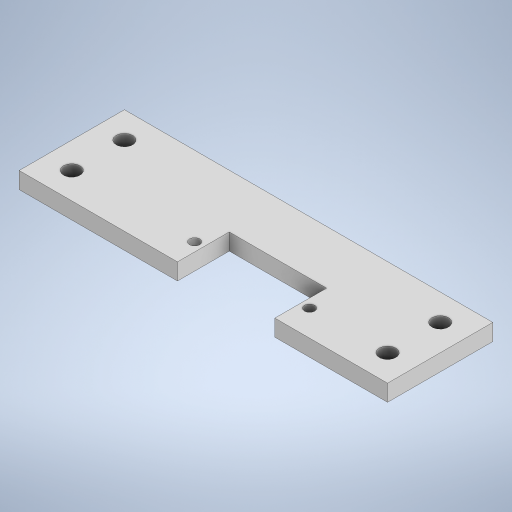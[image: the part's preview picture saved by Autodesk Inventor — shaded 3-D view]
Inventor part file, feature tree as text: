
AUTODESK INVENTOR PART (.ipt)
format: ipt  version: 2023.1 (Build 271208000, 208)  size: 259,584 bytes
history: native  units: mm
features: extrude x1, sketch x1
ambient origin geometry x8: Origin, YZ Plane, XZ Plane, XY Plane, X Axis, Y Axis, Z Axis, Center Point
bodies: Solid1 (feature_tree)
feature tree (2):
  extrude  "Extrusion1"  Depth=4.0mm
  sketch  "Sketch1"  dims[d0=25.4mm d1=76.2mm d2=12.7mm d3=88.9mm d4=6.35mm d5=6.35mm d6=4.0mm d7=4.0mm d8=4.0mm d9=4.0mm d11=32.0mm d12=23.5mm d13=12.5mm d14=2.5mm d15=2.5mm d16=23.0mm d17=6.0mm d18=4.0mm d19=0.0mm d20=0.0mm d21=0.0mm d22=0.0mm d23=0.0mm]
